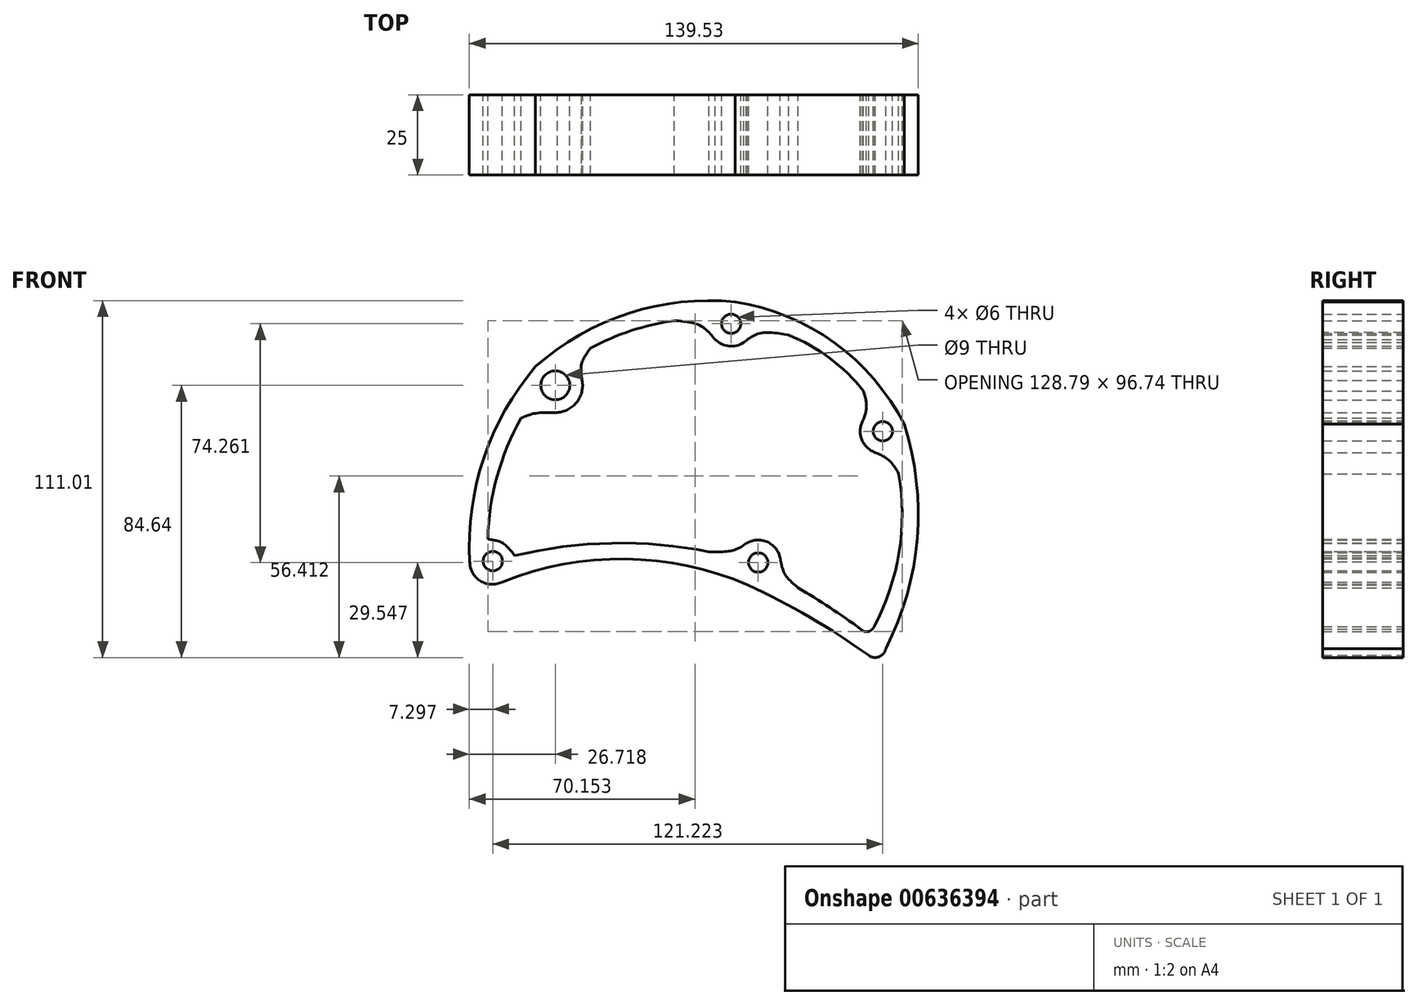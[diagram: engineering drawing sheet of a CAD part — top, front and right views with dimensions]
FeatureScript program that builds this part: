
annotation { "Feature Type Name" : "Feature", "Feature Type Description" : "" }
export const myFeature = defineFeature(function(context is Context, id is Id, definition is map)
    precondition{}
    {
        {
            var Q0;
            Q0=qCreatedBy(makeId("Front.planeOp"),FACE);
            var sketch = newSketch(context, id + "F0", { "sketchPlane" : qUnion([Q0])});
            skCircle(sketch, "E0", {"center": v(9.64, 53.23) * mm, "radius": 3 * mm});
            skCircle(sketch, "E1", {"center": v(56.78, 19.79) * mm, "radius": 3 * mm});
            skCircle(sketch, "E2", {"center": v(-64.44, -20.6) * mm, "radius": 3 * mm});
            skCircle(sketch, "E3", {"center": v(-45.02, 34.06) * mm, "radius": 4.5 * mm});
            skArc(sketch, "E4", {"start": v(-51.18, 39.87) * mm, "mid": v(-67.23, 11.54) * mm, "end": v(-71.6, -20.72) * mm});
            skArc(sketch, "E5", {"start": v(10.9, 60.03) * mm, "mid": v(-22.26, 56.47) * mm, "end": v(-51.18, 39.87) * mm});
            skArc(sketch, "E6", {"start": v(63.43, 21.98) * mm, "mid": v(41.73, 47.3) * mm, "end": v(10.9, 60.03) * mm});
            skArc(sketch, "E7", {"start": v(57.7, -47.79) * mm, "mid": v(67.48, -13.47) * mm, "end": v(63.43, 21.98) * mm});
            skCircle(sketch, "E8", {"center": v(18.04, -21.03) * mm, "radius": 3 * mm});
            skArc(sketch, "E9", {"start": v(14.8, -28) * mm, "mid": v(-23.25, -19.9) * mm, "end": v(-61.48, -27.07) * mm});
            skArc(sketch, "E10", {"start": v(52.37, -49.9) * mm, "mid": v(34.1, -38.07) * mm, "end": v(14.8, -28) * mm});
            skArc(sketch, "E11", {"start": v(52.37, -49.9) * mm, "mid": v(55.62, -50.34) * mm, "end": v(57.7, -47.79) * mm});
            skArc(sketch, "E12", {"start": v(-71.6, -20.72) * mm, "mid": v(-68.33, -26.74) * mm, "end": v(-61.48, -27.07) * mm});
            skFitSpline(sketch, "E13", {"points": [v(-65.98, -13.78) * mm, v(-61.38, -15) * mm, v(-57.64, -18.93) * mm], "startDerivative": vector(10.08, -1.32) * mm, "endDerivative": vector(6.65, -8.93) * mm});
            skFitSpline(sketch, "E14", {"points": [v(-55.67, 23.9) * mm, v(-50.47, 25.48) * mm, v(-44.8, 25.59) * mm, v(-44.41, 25.6) * mm], "startDerivative": vector(10.64, 4.54) * mm, "endDerivative": vector(2.23, 0.18) * mm});
            skFitSpline(sketch, "E15", {"points": [v(-34.08, 45.61) * mm, v(-36.8, 40.9) * mm, v(-36.7, 35.61) * mm], "startDerivative": vector(-6.84, -8.99) * mm, "endDerivative": vector(1.61, -10.98) * mm});
            skArc(sketch, "E16", {"start": v(-44.41, 25.6) * mm, "mid": v(-38.3, 28.87) * mm, "end": v(-36.7, 35.61) * mm});
            skArc(sketch, "E17", {"start": v(-55.67, 23.9) * mm, "mid": v(-63.12, 5.69) * mm, "end": v(-65.98, -13.78) * mm});
            skFitSpline(sketch, "E18", {"points": [v(-8.06, 54.2) * mm, v(0, 52.65) * mm, v(4.68, 48.29) * mm], "startDerivative": vector(16.56, -1.22) * mm, "endDerivative": vector(8.77, -10.8) * mm});
            skArc(sketch, "E19", {"start": v(-8.06, 54.2) * mm, "mid": v(-21.45, 51.05) * mm, "end": v(-34.08, 45.61) * mm});
            skFitSpline(sketch, "E20", {"points": [v(27.53, 49.68) * mm, v(18.7, 50.26) * mm, v(13.5, 47.37) * mm], "startDerivative": vector(-17.29, 3.21) * mm, "endDerivative": vector(-10.51, -8.1) * mm});
            skArc(sketch, "E21", {"start": v(4.68, 48.29) * mm, "mid": v(8.93, 46.26) * mm, "end": v(13.5, 47.37) * mm});
            skFitSpline(sketch, "E22", {"points": [v(50.8, 32.26) * mm, v(51.7, 27.26) * mm, v(50.56, 23) * mm], "startDerivative": vector(2.93, -9.81) * mm, "endDerivative": vector(-3.39, -8.64) * mm});
            skArc(sketch, "E23", {"start": v(50.8, 32.26) * mm, "mid": v(40.3, 42.5) * mm, "end": v(27.53, 49.68) * mm});
            skFitSpline(sketch, "E24", {"points": [v(61.74, 6.58) * mm, v(58.7, 10.74) * mm, v(54.46, 13.18) * mm], "startDerivative": vector(-5.18, 9.09) * mm, "endDerivative": vector(-9.25, 4.14) * mm});
            skArc(sketch, "E25", {"start": v(50.56, 23) * mm, "mid": v(50.25, 17.2) * mm, "end": v(54.46, 13.18) * mm});
            skArc(sketch, "E26", {"start": v(54.02, -41) * mm, "mid": v(61.85, -17.86) * mm, "end": v(61.74, 6.58) * mm});
            skArc(sketch, "E27", {"start": v(49.9, -41.72) * mm, "mid": v(52.16, -42.51) * mm, "end": v(54.02, -41) * mm});
            skFitSpline(sketch, "E28", {"points": [v(30.43, -28.89) * mm, v(26.3, -24.58) * mm, v(24.87, -19.5) * mm], "startDerivative": vector(-9.15, 8.03) * mm, "endDerivative": vector(-1.8, 10.95) * mm});
            skFitSpline(sketch, "E29", {"points": [v(2.8, -17.71) * mm, v(10.32, -17.21) * mm, v(14.34, -15.1) * mm], "startDerivative": vector(14.53, -0.22) * mm, "endDerivative": vector(8.28, 5.7) * mm});
            skArc(sketch, "E30", {"start": v(24.87, -19.5) * mm, "mid": v(20.75, -14.57) * mm, "end": v(14.34, -15.1) * mm});
            skArc(sketch, "E31", {"start": v(49.9, -41.72) * mm, "mid": v(40.34, -35.03) * mm, "end": v(30.43, -28.89) * mm});
            skArc(sketch, "E32", {"start": v(2.8, -17.71) * mm, "mid": v(-27.49, -15) * mm, "end": v(-57.64, -18.93) * mm});
            skSolve(sketch);
        }
        {
            var Q0;
            Q0 = qSketchRegion(id + "F0", true);
            extrude(context, id + "F1", {"entities" : qUnion([Q0]), "depth" : 25 * mm, "offsetDistance" : 25 * mm});
        }
    });
